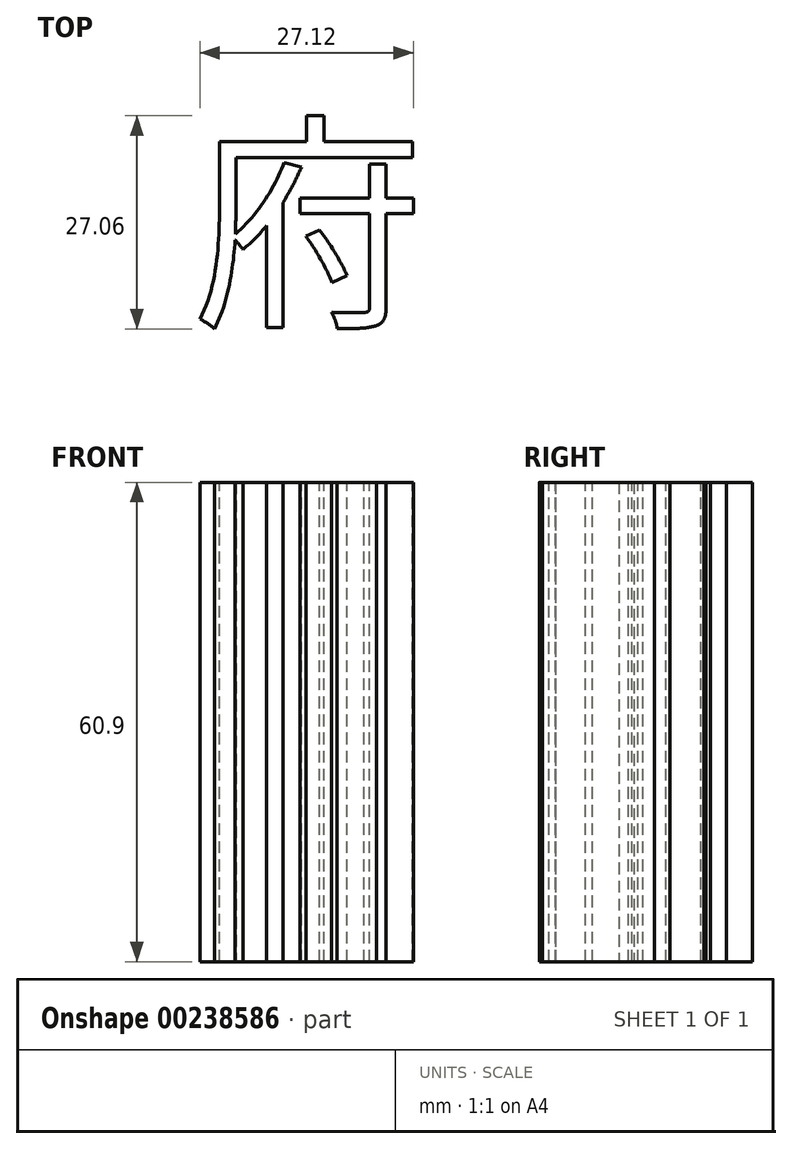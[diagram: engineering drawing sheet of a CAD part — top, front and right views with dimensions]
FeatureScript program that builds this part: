
annotation { "Feature Type Name" : "Feature", "Feature Type Description" : "" }
export const myFeature = defineFeature(function(context is Context, id is Id, definition is map)
    precondition{}
    {
        {
            var Q0;
            Q0=qCreatedBy(makeId("Front.planeOp"),FACE);
            var sketch = newSketch(context, id + "F0", { "sketchPlane" : qUnion([Q0])});
            skArc(sketch, "E0", {"start": v(0, -20) * mm, "mid": v(-20, 0) * mm, "end": v(0, 20) * mm});
            skLineSegment(sketch, "E1", {"start": v(0, 20) * mm, "end": v(0, -20) * mm, "construction": true});
            skSolve(sketch);
        }
        {
            var Q0;
            Q0=sQuery(id+"F0.wireOp",EDGE,"E0");
            var Q1;
            Q1=sQuery(id+"F0.wireOp",EDGE,"E1");
            revolve(context, id + "F1", {"bodyType" : ToolBodyType.SURFACE, "surfaceEntities" : qUnion([Q0]), "axis" : qUnion([Q1]), "revolveType" : RevolveType.FULL});
        }
        {
            var Q0;
            Q0=qCreatedBy(makeId("Top.planeOp"),FACE);
            cPlane(context, id + "F2", {"entities" : qUnion([Q0]), "cplaneType" : CPlaneType.OFFSET, "offset" : 50 * mm, "width" : 150 * mm, "height" : 150 * mm});
        }
        {
            var Q0;
            Q0=qCreatedBy(id+"F2.planeOp",FACE);
            var sketch = newSketch(context, id + "F3", { "sketchPlane" : qUnion([Q0])});
            skText(sketch, "E2", { "text": "府", "fontName": "NotoSansCJKjp-Regular.otf"});
            const initialGuessF3  = {"E2": [-0.01487, -0.01037, 1, 0, 0.02129]};
            skSetInitialGuess(sketch, initialGuessF3);
            skSolve(sketch);
        }
        {
            var Q0;
            Q0 = qSketchRegion(id + "F3", true);
            extrude(context, id + "F4", {"entities" : qUnion([Q0]), "oppositeDirection" : true, "depth" : 106.3 * mm, "hasSecondDirection" : true, "secondDirectionOppositeDirection" : true, "secondDirectionDepth" : 45.4 * mm});
        }
        {
            var Q0;
            Q0 = qConstructionFilter(qBodyType(qCreatedBy(id + "F3" ,EDGE), BodyType.WIRE), ConstructionObject.NO);
            extrude(context, id + "F5", {"bodyType" : ToolBodyType.SURFACE, "surfaceEntities" : qUnion([Q0]), "oppositeDirection" : true, "depth" : 47.7 * mm, "hasSecondDirection" : true, "secondDirectionOppositeDirection" : true, "secondDirectionDepth" : 45.5 * mm});
        }
        {
            var Q0;
            Q0=qCreatedBy(makeId("Top.planeOp"),FACE);
            cPlane(context, id + "F6", {"entities" : qUnion([Q0]), "cplaneType" : CPlaneType.OFFSET, "offset" : 15 * mm, "width" : 150 * mm, "height" : 150 * mm});
        }
    });
